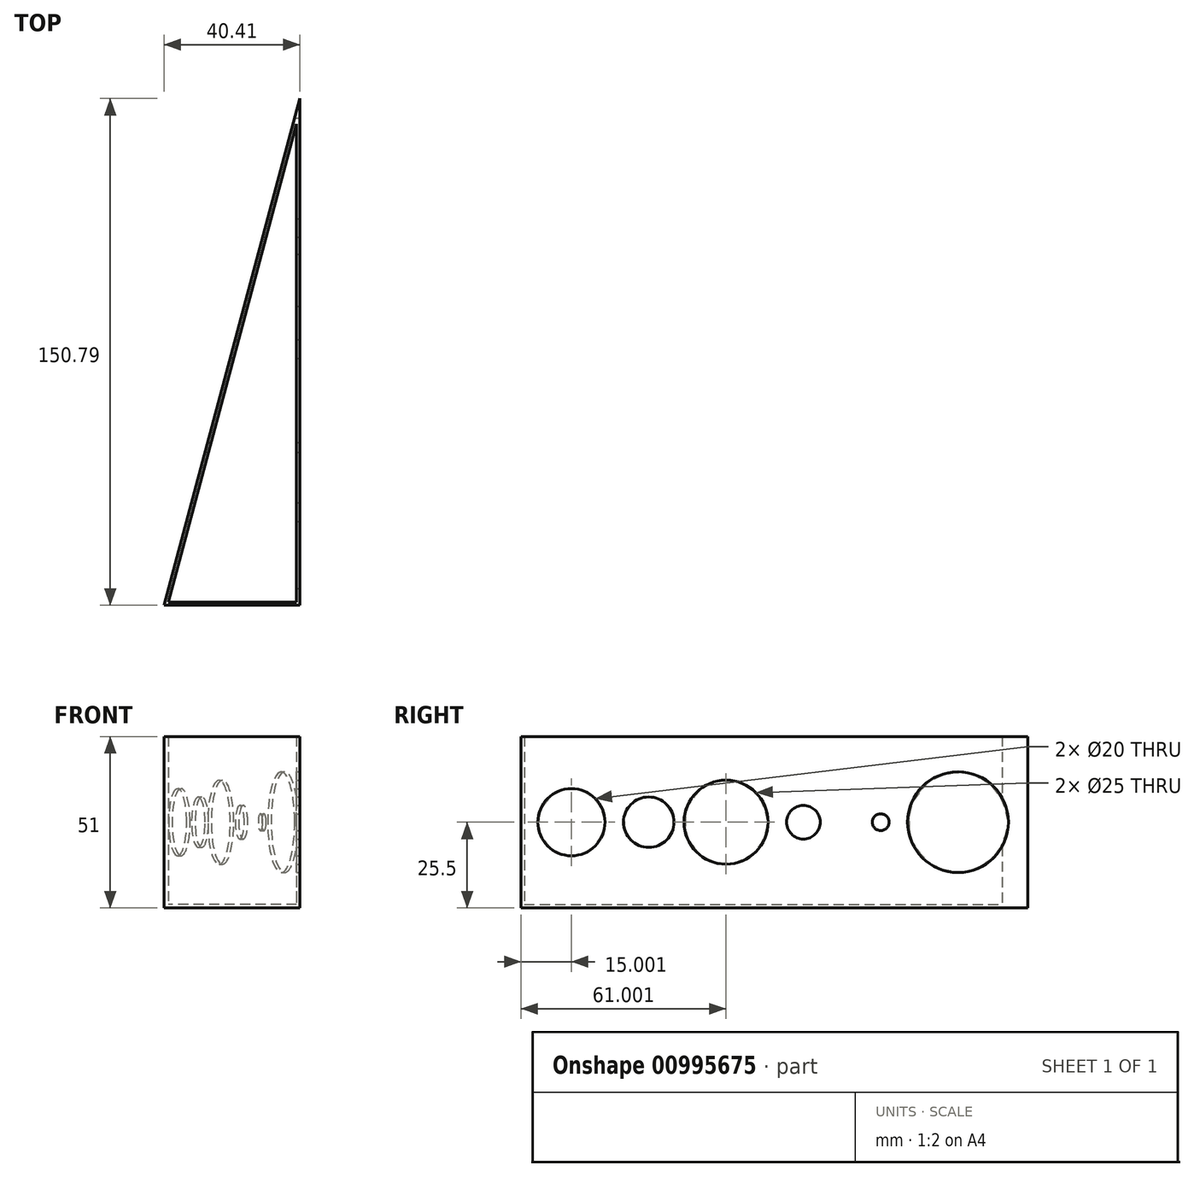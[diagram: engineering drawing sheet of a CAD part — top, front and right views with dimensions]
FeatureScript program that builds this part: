
annotation { "Feature Type Name" : "Feature", "Feature Type Description" : "" }
export const myFeature = defineFeature(function(context is Context, id is Id, definition is map)
    precondition{}
    {
        {
            var Q0;
            Q0=qCreatedBy(makeId("Top.planeOp"),FACE);
            var sketch = newSketch(context, id + "F0", { "sketchPlane" : qUnion([Q0])});
            skLineSegment(sketch, "E0", {"start": v(-20.92, 127.51) * mm, "end": v(-59.02, -14.68) * mm});
            skLineSegment(sketch, "E1", {"start": v(-59.02, -14.68) * mm, "end": v(-20.92, -14.68) * mm});
            skLineSegment(sketch, "E2", {"start": v(-20.92, -14.68) * mm, "end": v(-20.92, 127.51) * mm});
            skSolve(sketch);
        }
        {
            var Q0;
            Q0=makeQuery(id+"F0.imprint","IMPRINT",FACE,{"disambiguationData":[TD([[makeQuery(id+"F0.imprint","IMPRINT",EDGE,{"derivedFrom":sQuery(id+"F0.wireOp",EDGE,"E0")}),1.0]])]});
            extrude(context, id + "F1", {"entities" : qUnion([Q0]), "depth" : 50 * mm, "offsetDistance" : 25 * mm});
        }
        {
            var Q0;
            Q0=makeQuery(id+"F1.opExtrude","CAP_FACE",FACE,{"disambiguationData":[OSD([sQuery(id+"F0.wireOp",EDGE,"E0"),sQuery(id+"F0.wireOp",EDGE,"E1"),sQuery(id+"F0.wireOp",EDGE,"E2")])],"isStart":false});
            var Q1;
            Q1=makeQuery(id+"F1.opExtrude","SWEPT_BODY",BODY,{"disambiguationData":[OSD([sQuery(id+"F0.wireOp",EDGE,"E0"),sQuery(id+"F0.wireOp",EDGE,"E1"),sQuery(id+"F0.wireOp",EDGE,"E2")])]});
            shell(context, id + "F2", {"entities" : qUnion([Q0]), "parts" : qUnion([Q1]), "thickness" : 1 * mm, "oppositeDirection" : true});
        }
        {
            var Q0;
            Q0=makeQuery(id+"F1.opExtrude","SWEPT_FACE",FACE,{"disambiguationData":[OSD([sQuery(id+"F0.wireOp",EDGE,"E2")])]});
            var sketch = newSketch(context, id + "F3", { "sketchPlane" : qUnion([Q0])});
            skLineSegment(sketch, "E3", {"start": v(-15.68, 24.5) * mm, "end": v(135.1, 24.5) * mm, "construction": true});
            skPoint(sketch, "E4", {"position": v(-0.68, 24.5) * mm});
            skPoint(sketch, "E5.1.0.0", {"position": v(22.32, 24.5) * mm});
            skPoint(sketch, "E5.2.0.0", {"position": v(45.32, 24.5) * mm});
            skPoint(sketch, "E5.3.0.0", {"position": v(68.32, 24.5) * mm});
            skPoint(sketch, "E5.4.0.0", {"position": v(91.32, 24.5) * mm});
            skPoint(sketch, "E5.5.0.0", {"position": v(114.32, 24.5) * mm});
            skLineSegment(sketch, "E5.direction1", {"start": v(-0.68, 24.5) * mm, "end": v(22.32, 24.5) * mm, "construction": true});
            skSolve(sketch);
        }
        {
            var Q0;
            Q0=sQuery(id+"F3.wireOp",VERTEX,"E5.5.0.0");
            var Q1;
            Q1=makeQuery(id+"F1.opExtrude","SWEPT_BODY",BODY,{"disambiguationData":[OSD([sQuery(id+"F0.wireOp",EDGE,"E0"),sQuery(id+"F0.wireOp",EDGE,"E1"),sQuery(id+"F0.wireOp",EDGE,"E2")])]});
            hole(context, id + "F4", {"style" : HoleStyle.SIMPLE, "endStyle" : HoleEndStyle.THROUGH, "holeDiameter" : 30 * mm, "majorDiameter" : 5 * mm, "isTappedThrough" : true, "tappedDepth" : 12 * mm, "tapClearance" : 3, "locations" : qUnion([Q0]), "scope" : qUnion([Q1])});
        }
        {
            var Q0;
            Q0=sQuery(id+"F3.wireOp",VERTEX,"E4");
            var Q1;
            Q1=makeQuery(id+"F1.opExtrude","SWEPT_BODY",BODY,{"disambiguationData":[OSD([sQuery(id+"F0.wireOp",EDGE,"E0"),sQuery(id+"F0.wireOp",EDGE,"E1"),sQuery(id+"F0.wireOp",EDGE,"E2")])]});
            hole(context, id + "F5", {"style" : HoleStyle.SIMPLE, "endStyle" : HoleEndStyle.THROUGH, "holeDiameter" : 20 * mm, "majorDiameter" : 5 * mm, "isTappedThrough" : true, "tappedDepth" : 12 * mm, "tapClearance" : 3, "locations" : qUnion([Q0]), "scope" : qUnion([Q1])});
        }
        {
            var Q0;
            Q0=sQuery(id+"F3.wireOp",VERTEX,"E5.2.0.0");
            var Q1;
            Q1=makeQuery(id+"F1.opExtrude","SWEPT_BODY",BODY,{"disambiguationData":[OSD([sQuery(id+"F0.wireOp",EDGE,"E0"),sQuery(id+"F0.wireOp",EDGE,"E1"),sQuery(id+"F0.wireOp",EDGE,"E2")])]});
            hole(context, id + "F6", {"style" : HoleStyle.SIMPLE, "endStyle" : HoleEndStyle.THROUGH, "holeDiameter" : 25 * mm, "majorDiameter" : 5 * mm, "isTappedThrough" : true, "tappedDepth" : 12 * mm, "tapClearance" : 3, "locations" : qUnion([Q0]), "scope" : qUnion([Q1])});
        }
        {
            var Q0;
            Q0=sQuery(id+"F3.wireOp",VERTEX,"E5.3.0.0");
            var Q1;
            Q1=makeQuery(id+"F1.opExtrude","SWEPT_BODY",BODY,{"disambiguationData":[OSD([sQuery(id+"F0.wireOp",EDGE,"E0"),sQuery(id+"F0.wireOp",EDGE,"E1"),sQuery(id+"F0.wireOp",EDGE,"E2")])]});
            hole(context, id + "F7", {"style" : HoleStyle.SIMPLE, "endStyle" : HoleEndStyle.THROUGH, "holeDiameter" : 10 * mm, "majorDiameter" : 5 * mm, "isTappedThrough" : true, "tappedDepth" : 12 * mm, "tapClearance" : 3, "locations" : qUnion([Q0]), "scope" : qUnion([Q1])});
        }
        {
            var Q0;
            Q0=sQuery(id+"F3.wireOp",VERTEX,"E5.4.0.0");
            var Q1;
            Q1=makeQuery(id+"F1.opExtrude","SWEPT_BODY",BODY,{"disambiguationData":[OSD([sQuery(id+"F0.wireOp",EDGE,"E0"),sQuery(id+"F0.wireOp",EDGE,"E1"),sQuery(id+"F0.wireOp",EDGE,"E2")])]});
            hole(context, id + "F8", {"style" : HoleStyle.SIMPLE, "endStyle" : HoleEndStyle.THROUGH, "holeDiameter" : 5 * mm, "majorDiameter" : 5 * mm, "isTappedThrough" : true, "tappedDepth" : 12 * mm, "tapClearance" : 3, "locations" : qUnion([Q0]), "scope" : qUnion([Q1])});
        }
        {
            var Q0;
            Q0=sQuery(id+"F3.wireOp",VERTEX,"E5.1.0.0");
            var Q1;
            Q1=makeQuery(id+"F1.opExtrude","SWEPT_BODY",BODY,{"disambiguationData":[OSD([sQuery(id+"F0.wireOp",EDGE,"E0"),sQuery(id+"F0.wireOp",EDGE,"E1"),sQuery(id+"F0.wireOp",EDGE,"E2")])]});
            hole(context, id + "F9", {"style" : HoleStyle.SIMPLE, "endStyle" : HoleEndStyle.THROUGH, "holeDiameter" : 15 * mm, "majorDiameter" : 5 * mm, "isTappedThrough" : true, "tappedDepth" : 12 * mm, "tapClearance" : 3, "locations" : qUnion([Q0]), "scope" : qUnion([Q1])});
        }
    });
